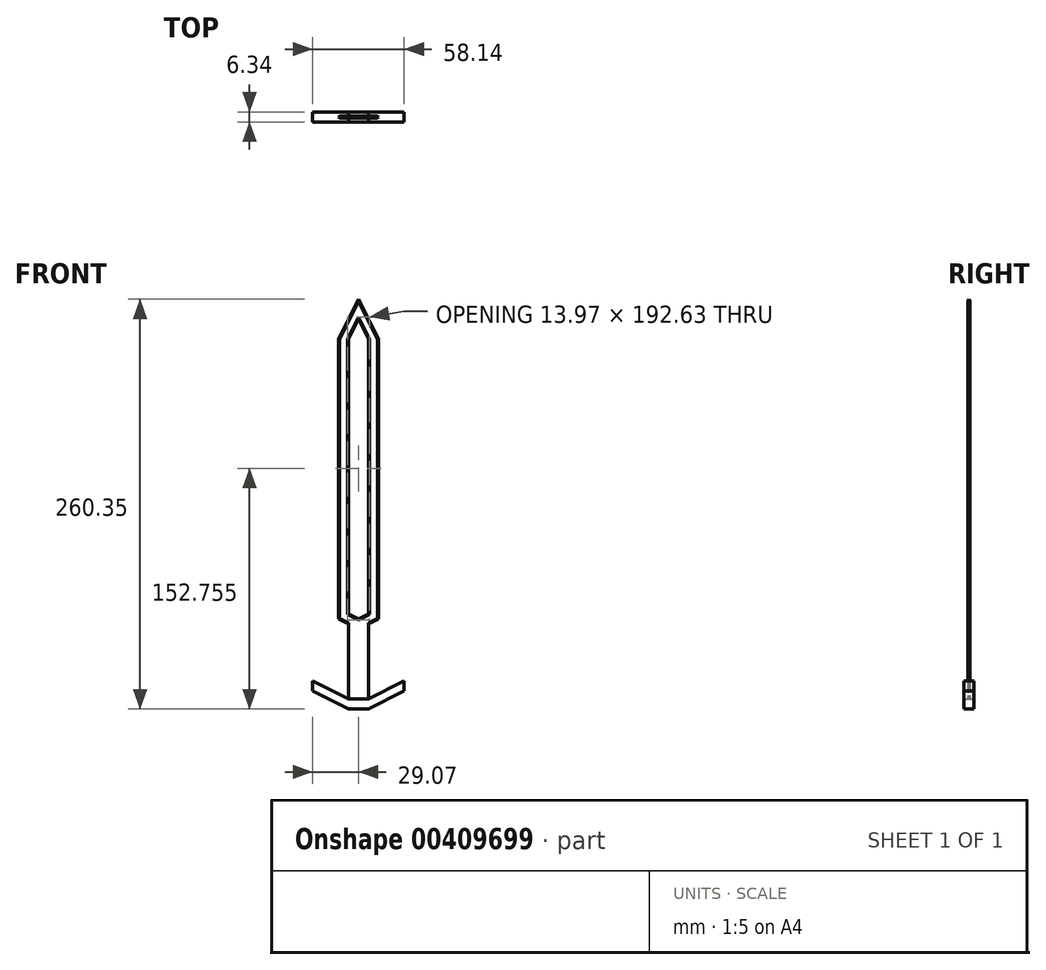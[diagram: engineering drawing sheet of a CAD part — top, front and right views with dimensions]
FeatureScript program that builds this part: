
annotation { "Feature Type Name" : "Feature", "Feature Type Description" : "" }
export const myFeature = defineFeature(function(context is Context, id is Id, definition is map)
    precondition{}
    {
        {
            var Q0;
            Q0=qCreatedBy(makeId("Front.planeOp"),FACE);
            var sketch = newSketch(context, id + "F0", { "sketchPlane" : qUnion([Q0])});
            skLineSegment(sketch, "E0", {"start": v(0, 203.2) * mm, "end": v(0, -57.15) * mm, "construction": true});
            skLineSegment(sketch, "E1", {"start": v(0, 203.2) * mm, "end": v(-12.7, 177.8) * mm});
            skLineSegment(sketch, "E2", {"start": v(-12.7, 177.8) * mm, "end": v(-12.7, 0) * mm});
            skLineSegment(sketch, "E3", {"start": v(-12.7, 0) * mm, "end": v(-6.35, -3.18) * mm});
            skLineSegment(sketch, "E4.MirrorCS", {"start": v(12.7, 0) * mm, "end": v(6.35, -3.18) * mm});
            skLineSegment(sketch, "E5.MirrorCS", {"start": v(0, 203.2) * mm, "end": v(12.7, 177.8) * mm});
            skLineSegment(sketch, "E6.MirrorCS", {"start": v(12.7, 177.8) * mm, "end": v(12.7, 0) * mm});
            skLineSegment(sketch, "E7", {"start": v(0, 190.5) * mm, "end": v(-6.35, 177.8) * mm});
            skLineSegment(sketch, "E8", {"start": v(-6.35, 177.8) * mm, "end": v(-6.35, 3.17) * mm});
            skPoint(sketch, "E9.MirrorCS.end.orphan", {"position": v(0, -50.8) * mm});
            skPoint(sketch, "E9.MirrorCS.start.orphan", {"position": v(6.35, -50.8) * mm});
            skPoint(sketch, "E10.start.orphan", {"position": v(-6.35, -50.8) * mm});
            skLineSegment(sketch, "E11", {"start": v(-6.35, -3.17) * mm, "end": v(-6.35, -50.8) * mm});
            skLineSegment(sketch, "E12", {"start": v(-6.35, -50.8) * mm, "end": v(0, -50.8) * mm});
            skLineSegment(sketch, "E13.MirrorCS", {"start": v(0, 190.5) * mm, "end": v(6.35, 177.8) * mm});
            skLineSegment(sketch, "E14.MirrorCS", {"start": v(6.35, -50.8) * mm, "end": v(0, -50.8) * mm});
            skLineSegment(sketch, "E15.MirrorCS", {"start": v(6.35, 177.8) * mm, "end": v(6.35, 3.18) * mm});
            skLineSegment(sketch, "E16.MirrorCS", {"start": v(6.35, -3.17) * mm, "end": v(6.35, -50.8) * mm});
            skLineSegment(sketch, "E17", {"start": v(-6.35, 3.17) * mm, "end": v(0, 0) * mm});
            skLineSegment(sketch, "E18", {"start": v(0, 0) * mm, "end": v(6.35, 3.17) * mm});
            skLineSegment(sketch, "E19", {"start": v(-6.35, -50.8) * mm, "end": v(-29.07, -39.44) * mm});
            skLineSegment(sketch, "E20", {"start": v(-29.07, -39.44) * mm, "end": v(-29.07, -45.8) * mm});
            skLineSegment(sketch, "E21", {"start": v(-29.07, -45.8) * mm, "end": v(-6.35, -57.15) * mm});
            skLineSegment(sketch, "E22", {"start": v(-6.35, -57.15) * mm, "end": v(0, -57.15) * mm});
            skLineSegment(sketch, "E23.MirrorCS", {"start": v(6.35, -57.15) * mm, "end": v(0, -57.15) * mm});
            skLineSegment(sketch, "E24.MirrorCS", {"start": v(29.07, -45.8) * mm, "end": v(6.35, -57.15) * mm});
            skLineSegment(sketch, "E25.MirrorCS", {"start": v(6.35, -50.8) * mm, "end": v(29.07, -39.44) * mm});
            skLineSegment(sketch, "E26.MirrorCS", {"start": v(29.07, -39.44) * mm, "end": v(29.07, -45.8) * mm});
            skLineSegment(sketch, "E27", {"start": v(-3.17, -57.15) * mm, "end": v(-3.17, -82.55) * mm});
            skPoint(sketch, "E28.endSnap0", {"position": v(3.17, -57.15) * mm});
            skArc(sketch, "E29", {"start": v(-3.18, -82.55) * mm, "mid": v(-2.98, -83.65) * mm, "end": v(-2.41, -84.61) * mm});
            skLineSegment(sketch, "E30.trimOffspring", {"start": v(0, -85.72) * mm, "end": v(0, -205.54) * mm, "construction": true});
            skPoint(sketch, "E31", {"position": v(0, -84.14) * mm});
            skArc(sketch, "E32", {"start": v(-2.41, -84.61) * mm, "mid": v(-6.23, -91.72) * mm, "end": v(0, -96.84) * mm});
            skLineSegment(sketch, "E33", {"start": v(-3.17, -82.55) * mm, "end": v(0, -82.55) * mm});
            skLineSegment(sketch, "E34", {"start": v(3.17, -57.15) * mm, "end": v(3.17, -82.55) * mm});
            skLineSegment(sketch, "E35", {"start": v(3.18, -82.55) * mm, "end": v(0, -82.55) * mm});
            skSolve(sketch);
        }
        {
            var Q0;
            Q0=makeQuery(id+"F0.imprint","IMPRINT",FACE,{"disambiguationData":[TD([[makeQuery(id+"F0.imprint","IMPRINT",EDGE,{"derivedFrom":sQuery(id+"F0.wireOp",EDGE,"E1")}),1.0]])]});
            extrude(context, id + "F1", {"entities" : qUnion([Q0]), "endBound" : BoundingType.SYMMETRIC, "depth" : 1.27 * mm});
        }
        {
            var Q0;
            Q0=makeQuery(id+"F1.opExtrude","CAP_EDGE",EDGE,{"disambiguationData":[OSD([sQuery(id+"F0.wireOp",EDGE,"E6.MirrorCS")])],"isStart":false});
            var Q1;
            Q1=makeQuery(id+"F1.opExtrude","CAP_EDGE",EDGE,{"disambiguationData":[OSD([sQuery(id+"F0.wireOp",EDGE,"E5.MirrorCS")])],"isStart":false});
            var Q2;
            Q2=makeQuery(id+"F1.opExtrude","CAP_EDGE",EDGE,{"disambiguationData":[OSD([sQuery(id+"F0.wireOp",EDGE,"E1")])],"isStart":false});
            var Q3;
            Q3=makeQuery(id+"F1.opExtrude","CAP_EDGE",EDGE,{"disambiguationData":[OSD([sQuery(id+"F0.wireOp",EDGE,"E2")])],"isStart":false});
            var Q4;
            Q4=makeQuery(id+"F1.opExtrude","CAP_EDGE",EDGE,{"disambiguationData":[OSD([sQuery(id+"F0.wireOp",EDGE,"E3")])],"isStart":false});
            var Q5;
            Q5=makeQuery(id+"F1.opExtrude","CAP_EDGE",EDGE,{"disambiguationData":[OSD([sQuery(id+"F0.wireOp",EDGE,"E4.MirrorCS")])],"isStart":false});
            var Q6;
            Q6=makeQuery(id+"F1.opExtrude","CAP_EDGE",EDGE,{"disambiguationData":[OSD([sQuery(id+"F0.wireOp",EDGE,"E3")])],"isStart":true});
            var Q7;
            Q7=makeQuery(id+"F1.opExtrude","CAP_EDGE",EDGE,{"disambiguationData":[OSD([sQuery(id+"F0.wireOp",EDGE,"E4.MirrorCS")])],"isStart":true});
            var Q8;
            Q8=makeQuery(id+"F1.opExtrude","CAP_EDGE",EDGE,{"disambiguationData":[OSD([sQuery(id+"F0.wireOp",EDGE,"E2")])],"isStart":true});
            var Q9;
            Q9=makeQuery(id+"F1.opExtrude","CAP_EDGE",EDGE,{"disambiguationData":[OSD([sQuery(id+"F0.wireOp",EDGE,"E6.MirrorCS")])],"isStart":true});
            var Q10;
            Q10=makeQuery(id+"F1.opExtrude","CAP_EDGE",EDGE,{"disambiguationData":[OSD([sQuery(id+"F0.wireOp",EDGE,"E1")])],"isStart":true});
            var Q11;
            Q11=makeQuery(id+"F1.opExtrude","CAP_EDGE",EDGE,{"disambiguationData":[OSD([sQuery(id+"F0.wireOp",EDGE,"E5.MirrorCS")])],"isStart":true});
            chamfer(context, id + "F2", {"entities" : qUnion([Q0, Q1, Q2, Q3, Q4, Q5, Q6, Q7, Q8, Q9, Q10, Q11]), "width" : 0.64 * mm, "tangentPropagation" : true});
        }
        {
            var Q0;
            Q0=makeQuery(id+"F0.imprint","IMPRINT",FACE,{"disambiguationData":[TD([[makeQuery(id+"F0.imprint","IMPRINT",EDGE,{"derivedFrom":sQuery(id+"F0.wireOp",EDGE,"E12")}),-1.0]])]});
            extrude(context, id + "F3", {"entities" : qUnion([Q0]), "operationType" : NewBodyOperationType.ADD, "endBound" : BoundingType.SYMMETRIC, "depth" : 6.35 * mm});
        }
        {
            var Q0;
            Q0=makeQuery(id+"F1.opExtrude","CAP_EDGE",EDGE,{"disambiguationData":[OSD([sQuery(id+"F0.wireOp",EDGE,"E15.MirrorCS")])],"isStart":false});
            var Q1;
            Q1=makeQuery(id+"F1.opExtrude","CAP_EDGE",EDGE,{"disambiguationData":[OSD([sQuery(id+"F0.wireOp",EDGE,"E8")])],"isStart":false});
            var Q2;
            Q2=makeQuery(id+"F1.opExtrude","CAP_EDGE",EDGE,{"disambiguationData":[OSD([sQuery(id+"F0.wireOp",EDGE,"E18")])],"isStart":false});
            var Q3;
            Q3=makeQuery(id+"F1.opExtrude","CAP_EDGE",EDGE,{"disambiguationData":[OSD([sQuery(id+"F0.wireOp",EDGE,"E17")])],"isStart":false});
            var Q4;
            Q4=makeQuery(id+"F1.opExtrude","CAP_EDGE",EDGE,{"disambiguationData":[OSD([sQuery(id+"F0.wireOp",EDGE,"E7")])],"isStart":false});
            var Q5;
            Q5=makeQuery(id+"F1.opExtrude","CAP_EDGE",EDGE,{"disambiguationData":[OSD([sQuery(id+"F0.wireOp",EDGE,"E13.MirrorCS")])],"isStart":false});
            var Q6;
            Q6=makeQuery(id+"F1.opExtrude","CAP_EDGE",EDGE,{"disambiguationData":[OSD([sQuery(id+"F0.wireOp",EDGE,"E13.MirrorCS")])],"isStart":true});
            var Q7;
            Q7=makeQuery(id+"F1.opExtrude","CAP_EDGE",EDGE,{"disambiguationData":[OSD([sQuery(id+"F0.wireOp",EDGE,"E7")])],"isStart":true});
            var Q8;
            Q8=makeQuery(id+"F1.opExtrude","CAP_EDGE",EDGE,{"disambiguationData":[OSD([sQuery(id+"F0.wireOp",EDGE,"E8")])],"isStart":true});
            var Q9;
            Q9=makeQuery(id+"F1.opExtrude","CAP_EDGE",EDGE,{"disambiguationData":[OSD([sQuery(id+"F0.wireOp",EDGE,"E15.MirrorCS")])],"isStart":true});
            var Q10;
            Q10=makeQuery(id+"F1.opExtrude","CAP_EDGE",EDGE,{"disambiguationData":[OSD([sQuery(id+"F0.wireOp",EDGE,"E17")])],"isStart":true});
            var Q11;
            Q11=makeQuery(id+"F1.opExtrude","CAP_EDGE",EDGE,{"disambiguationData":[OSD([sQuery(id+"F0.wireOp",EDGE,"E18")])],"isStart":true});
            chamfer(context, id + "F4", {"entities" : qUnion([Q0, Q1, Q2, Q3, Q4, Q5, Q6, Q7, Q8, Q9, Q10, Q11]), "width" : 0.64 * mm, "tangentPropagation" : true});
        }
    });
